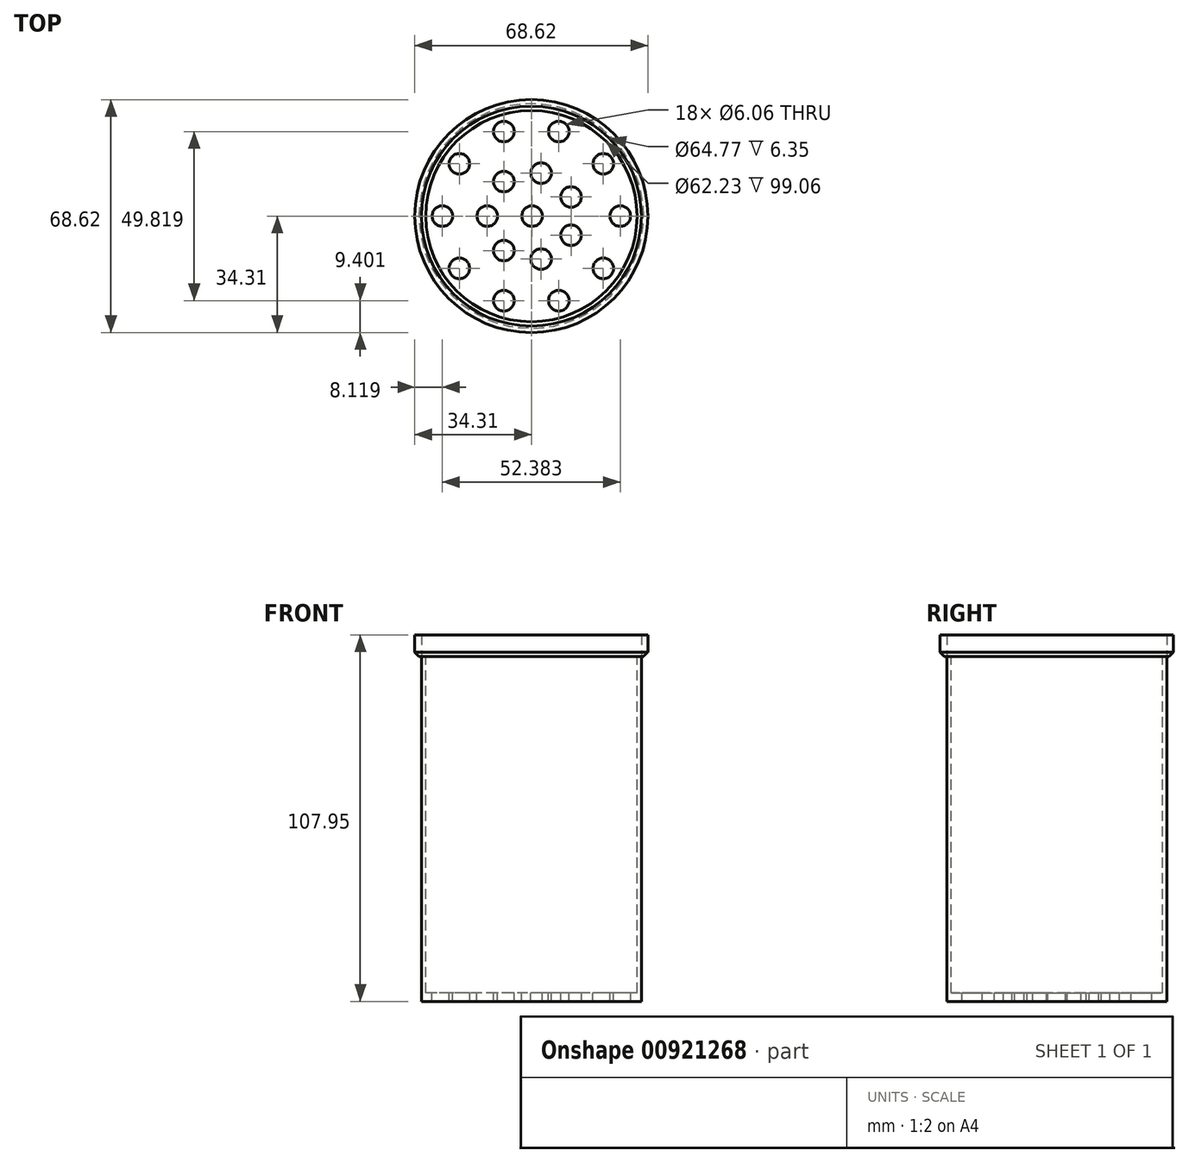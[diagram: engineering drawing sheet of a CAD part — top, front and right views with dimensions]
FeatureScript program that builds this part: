
annotation { "Feature Type Name" : "Feature", "Feature Type Description" : "" }
export const myFeature = defineFeature(function(context is Context, id is Id, definition is map)
    precondition{}
    {
        {
            var Q0;
            Q0=qCreatedBy(makeId("Top.planeOp"),FACE);
            var sketch = newSketch(context, id + "F0", { "sketchPlane" : qUnion([Q0])});
            skCircle(sketch, "E0", {"center": v(0, 0) * mm, "radius": 32.39 * mm});
            skSolve(sketch);
        }
        {
            var Q0;
            Q0=makeQuery(id+"F0.imprint","IMPRINT",FACE,{"disambiguationData":[TD([[makeQuery(id+"F0.imprint","IMPRINT",EDGE,{"derivedFrom":sQuery(id+"F0.wireOp",EDGE,"E0")}),1.0]])]});
            var Q1;
            Q1=sQuery(id+"F0.wireOp",EDGE,"E0");
            extrude(context, id + "F1", {"entities" : qUnion([Q0]), "surfaceEntities" : qUnion([Q1]), "depth" : 101.6 * mm, "offsetDistance" : 25.4 * mm});
        }
        {
            var Q0;
            Q0=makeQuery(id+"F1.opExtrude","CAP_FACE",FACE,{"disambiguationData":[OSD([sQuery(id+"F0.wireOp",EDGE,"E0")])],"isStart":false});
            var sketch = newSketch(context, id + "F2", { "sketchPlane" : qUnion([Q0])});
            skCircle(sketch, "E1", {"center": v(0, 0) * mm, "radius": 31.12 * mm});
            skSolve(sketch);
        }
        {
            var Q0;
            Q0=makeQuery(id+"F2.imprint","IMPRINT",FACE,{"disambiguationData":[TD([[makeQuery(id+"F2.imprint","IMPRINT",EDGE,{"derivedFrom":sQuery(id+"F2.wireOp",EDGE,"E1")}),1.0]])]});
            var Q1;
            Q1=sQuery(id+"F2.wireOp",EDGE,"E1");
            extrude(context, id + "F3", {"entities" : qUnion([Q0]), "operationType" : NewBodyOperationType.REMOVE, "surfaceEntities" : qUnion([Q1]), "oppositeDirection" : true, "depth" : 99.06 * mm, "offsetDistance" : 25.4 * mm});
        }
        {
            var Q0;
            Q0=makeQuery(id+"F0.imprint","IMPRINT",FACE,{"disambiguationData":[TD([[makeQuery(id+"F0.imprint","IMPRINT",EDGE,{"derivedFrom":sQuery(id+"F0.wireOp",EDGE,"E0")}),1.0]])]});
            var sketch = newSketch(context, id + "F4", { "sketchPlane" : qUnion([Q0])});
            skCircle(sketch, "E2", {"center": v(-26.2, 0) * mm, "radius": 3.03 * mm});
            skCircle(sketch, "E3.1.0.0", {"center": v(-12.98, 0) * mm, "radius": 3.03 * mm});
            skCircle(sketch, "E3.2.0.0", {"center": v(0.22, 0) * mm, "radius": 3.03 * mm});
            skLineSegment(sketch, "E3.direction1", {"start": v(-26.2, 0) * mm, "end": v(-12.98, 0) * mm, "construction": true});
            skCircle(sketch, "E4.1.0", {"center": v(-21.19, -15.4) * mm, "radius": 3.03 * mm});
            skCircle(sketch, "E4.2.0", {"center": v(-8.1, -24.9) * mm, "radius": 3.03 * mm});
            skCircle(sketch, "E4.3.0", {"center": v(8.1, -24.9) * mm, "radius": 3.03 * mm});
            skCircle(sketch, "E4.4.0", {"center": v(21.19, -15.4) * mm, "radius": 3.03 * mm});
            skCircle(sketch, "E4.5.0", {"center": v(26.2, 0) * mm, "radius": 3.03 * mm});
            skCircle(sketch, "E4.6.0", {"center": v(21.19, 15.4) * mm, "radius": 3.03 * mm});
            skCircle(sketch, "E4.7.0", {"center": v(8.1, 24.9) * mm, "radius": 3.03 * mm});
            skCircle(sketch, "E4.8.0", {"center": v(-8.1, 24.9) * mm, "radius": 3.03 * mm});
            skCircle(sketch, "E4.9.0", {"center": v(-21.19, 15.4) * mm, "radius": 3.03 * mm});
            skPoint(sketch, "E4.center", {"position": v(0, 0) * mm});
            skCircle(sketch, "E5.1.0", {"center": v(-8.1, -10.15) * mm, "radius": 3.03 * mm});
            skCircle(sketch, "E5.2.0", {"center": v(2.89, -12.66) * mm, "radius": 3.03 * mm});
            skCircle(sketch, "E5.3.0", {"center": v(11.7, -5.63) * mm, "radius": 3.03 * mm});
            skCircle(sketch, "E5.4.0", {"center": v(11.7, 5.63) * mm, "radius": 3.03 * mm});
            skCircle(sketch, "E5.5.0", {"center": v(2.89, 12.66) * mm, "radius": 3.03 * mm});
            skCircle(sketch, "E5.6.0", {"center": v(-8.1, 10.15) * mm, "radius": 3.03 * mm});
            skSolve(sketch);
        }
        {
            var Q0;
            Q0 = qSketchRegion(id + "F4", true);
            var Q1;
            Q1=sQuery(id+"F4.wireOp",EDGE,"E5.5.0");
            var Q2;
            Q2=sQuery(id+"F4.wireOp",EDGE,"E5.6.0");
            var Q3;
            Q3=sQuery(id+"F4.wireOp",EDGE,"E3.1.0.0");
            var Q4;
            Q4=sQuery(id+"F4.wireOp",EDGE,"E5.1.0");
            var Q5;
            Q5=sQuery(id+"F4.wireOp",EDGE,"E5.2.0");
            var Q6;
            Q6=sQuery(id+"F4.wireOp",EDGE,"E5.3.0");
            var Q7;
            Q7=sQuery(id+"F4.wireOp",EDGE,"E5.4.0");
            var Q8;
            Q8=sQuery(id+"F4.wireOp",EDGE,"E3.2.0.0");
            extrude(context, id + "F5", {"entities" : qUnion([Q0]), "operationType" : NewBodyOperationType.REMOVE, "surfaceEntities" : qUnion([Q1, Q2, Q3, Q4, Q5, Q6, Q7, Q8]), "oppositeDirection" : true, "depth" : 88.9 * mm, "offsetDistance" : 25.4 * mm, "hasSecondDirection" : true, "secondDirectionOppositeDirection" : false, "secondDirectionDepth" : 6.35 * mm});
        }
        {
            var Q0;
            Q0=makeQuery(id+"F1.opExtrude","CAP_FACE",FACE,{"disambiguationData":[OSD([sQuery(id+"F0.wireOp",EDGE,"E0")])],"isStart":false});
            var sketch = newSketch(context, id + "F6", { "sketchPlane" : qUnion([Q0])});
            skCircle(sketch, "E6", {"center": v(0, 0) * mm, "radius": 34.31 * mm});
            skSolve(sketch);
        }
        {
            var Q0;
            Q0=makeQuery(id+"F6.imprint","IMPRINT",FACE,{"disambiguationData":[TD([[makeQuery(id+"F6.imprint","IMPRINT",EDGE,{"derivedFrom":sQuery(id+"F6.wireOp",EDGE,"E6")}),1.0]])]});
            extrude(context, id + "F7", {"entities" : qUnion([Q0]), "depth" : 6.35 * mm, "offsetDistance" : 25.4 * mm});
        }
        {
            var Q0;
            Q0=makeQuery(id+"F7.opExtrude","CAP_EDGE",EDGE,{"disambiguationData":[OSD([sQuery(id+"F6.wireOp",EDGE,"E6")])],"isStart":true});
            chamfer(context, id + "F8", {"entities" : qUnion([Q0]), "width" : 1.27 * mm, "tangentPropagation" : true});
        }
    });
